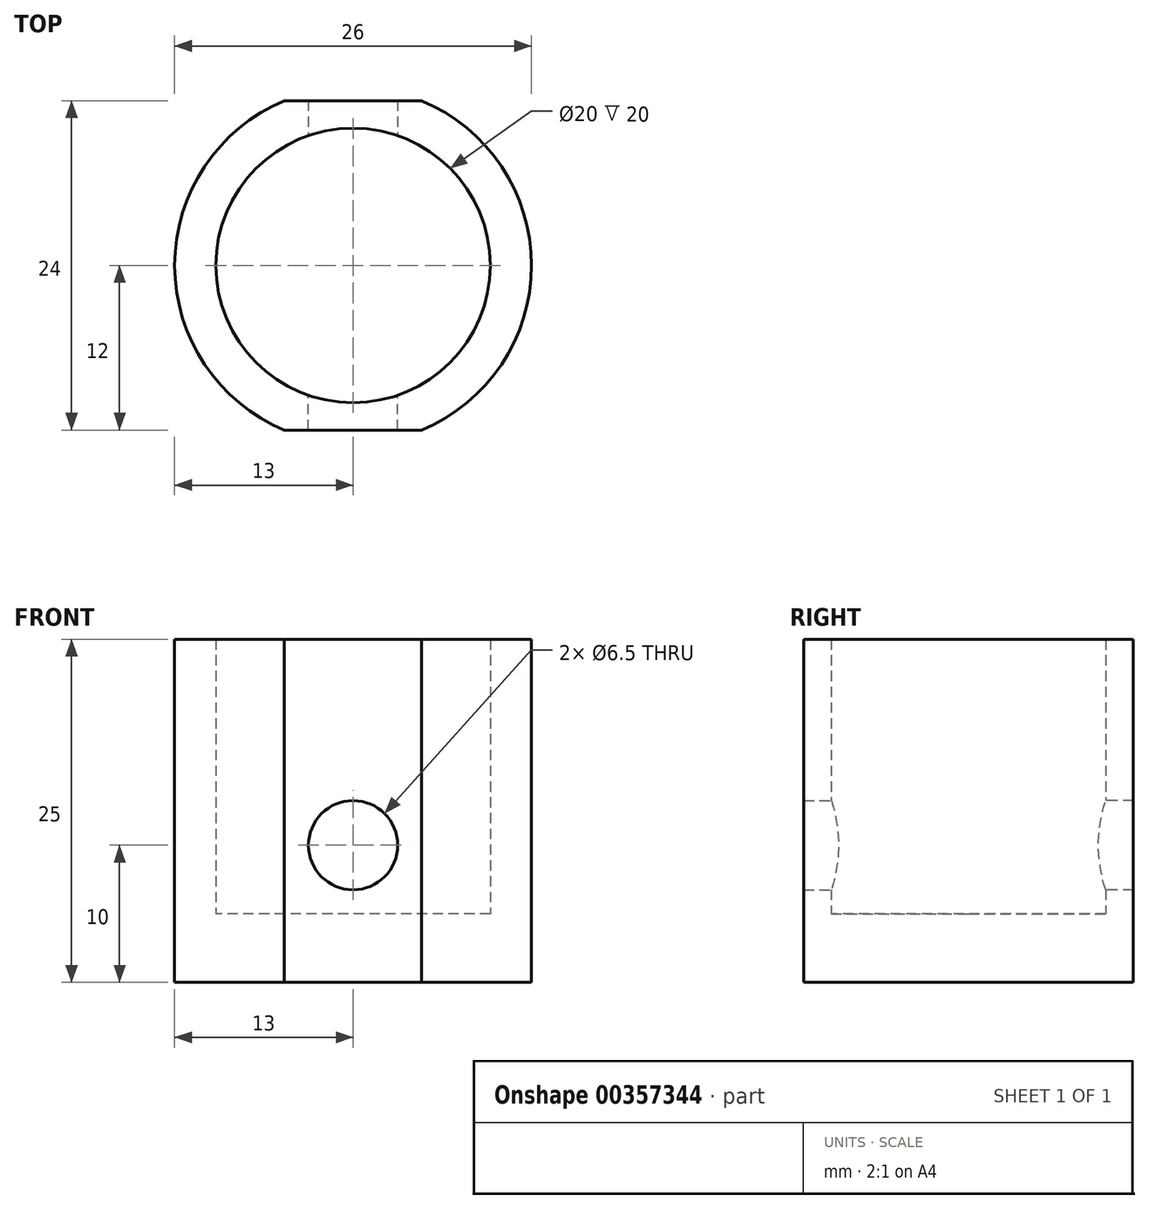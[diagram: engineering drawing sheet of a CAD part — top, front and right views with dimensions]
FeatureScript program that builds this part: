
annotation { "Feature Type Name" : "Feature", "Feature Type Description" : "" }
export const myFeature = defineFeature(function(context is Context, id is Id, definition is map)
    precondition{}
    {
        {
            var Q0;
            Q0=qCreatedBy(makeId("Top.planeOp"),FACE);
            var sketch = newSketch(context, id + "F0", { "sketchPlane" : qUnion([Q0])});
            skCircle(sketch, "E0", {"center": v(0, 0) * mm, "radius": 13 * mm});
            skCircle(sketch, "E1", {"center": v(0, 0) * mm, "radius": 10 * mm});
            skLineSegment(sketch, "E2", {"start": v(-5, 12) * mm, "end": v(5, 12) * mm});
            skLineSegment(sketch, "E3", {"start": v(-5, -12) * mm, "end": v(5, -12) * mm});
            skSolve(sketch);
        }
        {
            var Q0;
            Q0=makeQuery(id+"F0.imprint","IMPRINT",FACE,{"disambiguationData":[TD([[makeQuery(id+"F0.imprint","IMPRINT",EDGE,{"derivedFrom":sQuery(id+"F0.wireOp",EDGE,"E1")}),1.0]])]});
            var Q1;
            Q1=makeQuery(id+"F0.imprint","IMPRINT",FACE,{"disambiguationData":[TD([[makeQuery(id+"F0.imprint","IMPRINT",EDGE,{"derivedFrom":sQuery(id+"F0.wireOp",EDGE,"E0")}),1.0]])]});
            extrude(context, id + "F1", {"entities" : qUnion([Q0, Q1]), "depth" : 5 * mm});
        }
        {
            var Q0;
            Q0=makeQuery(id+"F0.imprint","IMPRINT",FACE,{"disambiguationData":[TD([[makeQuery(id+"F0.imprint","IMPRINT",EDGE,{"derivedFrom":sQuery(id+"F0.wireOp",EDGE,"E0")}),1.0]])]});
            extrude(context, id + "F2", {"entities" : qUnion([Q0]), "operationType" : NewBodyOperationType.ADD, "depth" : 25 * mm});
        }
        {
            var Q0;
            Q0=qCreatedBy(makeId("Front.planeOp"),FACE);
            var sketch = newSketch(context, id + "F3", { "sketchPlane" : qUnion([Q0])});
            skCircle(sketch, "E4", {"center": v(0, 10) * mm, "radius": 3.25 * mm});
            skSolve(sketch);
        }
        {
            var Q0;
            Q0=sQuery(id+"F3.wireOp",VERTEX,"E4.center");
            var Q1;
            Q1=makeQuery(id+"F1.opExtrude","SWEPT_BODY",BODY,{"disambiguationData":[OSD([sQuery(id+"F0.wireOp",EDGE,"E0")])]});
            hole(context, id + "F4", {"style" : HoleStyle.SIMPLE, "endStyle" : HoleEndStyle.THROUGH, "holeDiameter" : 6.5 * mm, "isTappedThrough" : true, "tappedDepth" : 12 * mm, "tapClearance" : 3, "locations" : qUnion([Q0]), "scope" : qUnion([Q1])});
        }
        {
            var Q0;
            Q0=qCreatedBy(makeId("Front.planeOp"),FACE);
            var sketch = newSketch(context, id + "F5", { "sketchPlane" : qUnion([Q0])});
            skCircle(sketch, "E5", {"center": v(0, 10) * mm, "radius": 3.25 * mm});
            skSolve(sketch);
        }
        {
            var Q0;
            Q0=sQuery(id+"F5.wireOp",VERTEX,"E5.center");
            var Q1;
            Q1=makeQuery(id+"F1.opExtrude","SWEPT_BODY",BODY,{"disambiguationData":[OSD([sQuery(id+"F0.wireOp",EDGE,"E0")])]});
            hole(context, id + "F6", {"style" : HoleStyle.SIMPLE, "endStyle" : HoleEndStyle.THROUGH, "oppositeDirection" : true, "holeDiameter" : 6.5 * mm, "isTappedThrough" : true, "tappedDepth" : 12 * mm, "tapClearance" : 3, "locations" : qUnion([Q0]), "scope" : qUnion([Q1])});
        }
    });
